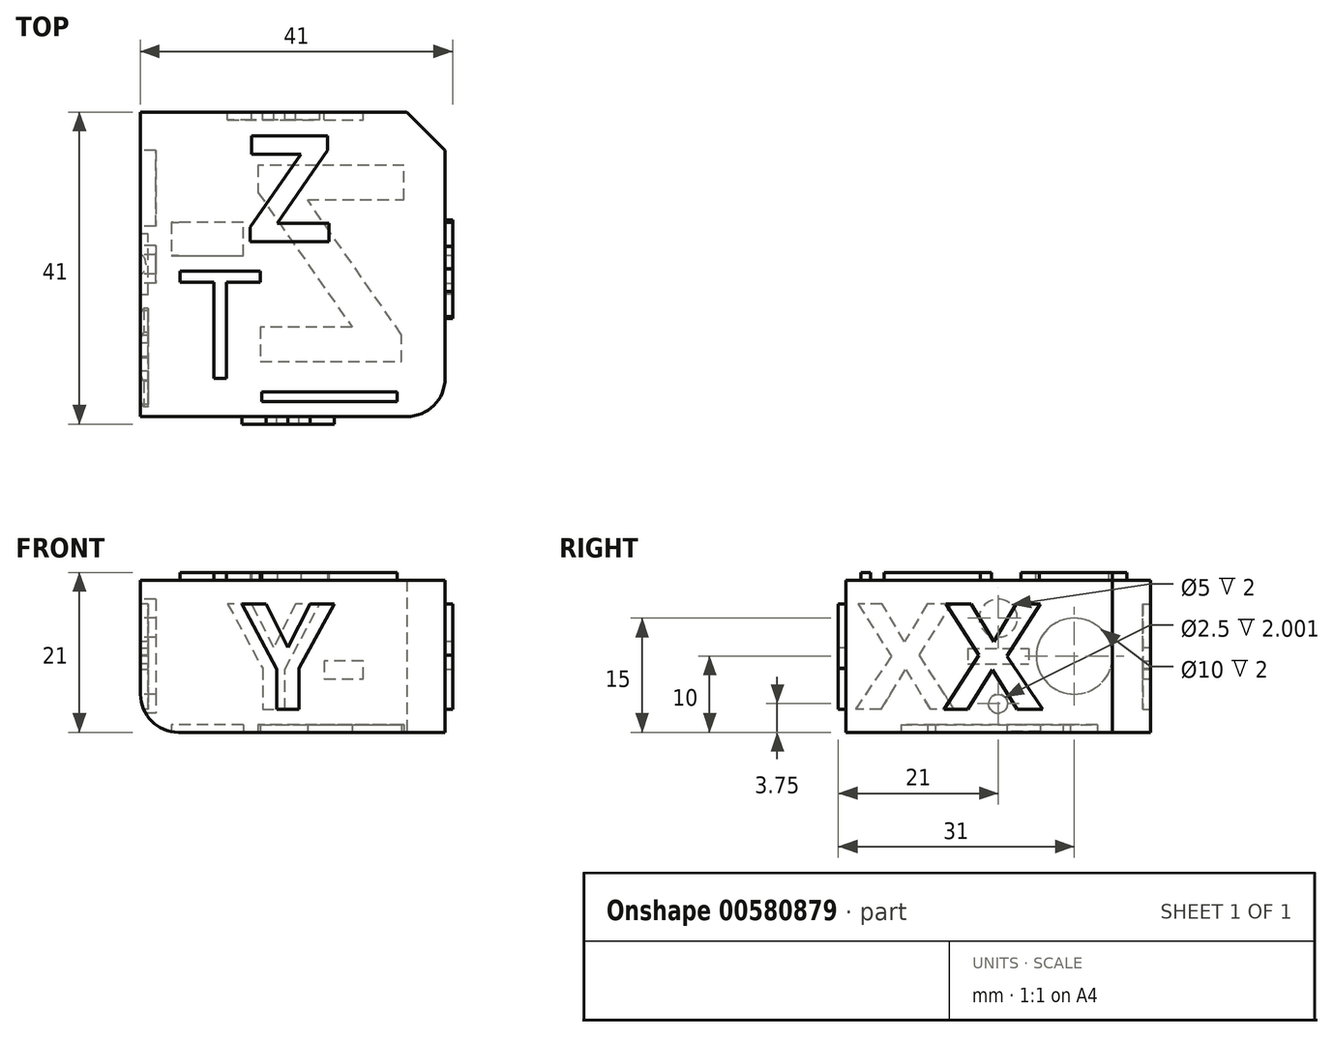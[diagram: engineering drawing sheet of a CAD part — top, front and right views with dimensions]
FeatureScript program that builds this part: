
annotation { "Feature Type Name" : "Feature", "Feature Type Description" : "" }
export const myFeature = defineFeature(function(context is Context, id is Id, definition is map)
    precondition{}
    {
        {
            var Q0;
            Q0=qCreatedBy(makeId("Top.planeOp"),FACE);
            var sketch = newSketch(context, id + "F0", { "sketchPlane" : qUnion([Q0])});
            skLineSegment(sketch, "E0.bottom", {"start": v(20, 20) * mm, "end": v(-20, 20) * mm});
            skLineSegment(sketch, "E0.top", {"start": v(20, -20) * mm, "end": v(-20, -20) * mm});
            skLineSegment(sketch, "E0.left", {"start": v(20, 20) * mm, "end": v(20, -20) * mm});
            skLineSegment(sketch, "E0.right", {"start": v(-20, 20) * mm, "end": v(-20, -20) * mm});
            skPoint(sketch, "E0.middle", {"position": v(0, 0) * mm});
            skSolve(sketch);
        }
        {
            var Q0;
            Q0=makeQuery(id+"F0.imprint","IMPRINT",FACE,{"disambiguationData":[TD([[makeQuery(id+"F0.imprint","IMPRINT",EDGE,{"derivedFrom":sQuery(id+"F0.wireOp",EDGE,"E0.bottom")}),1.0]])]});
            extrude(context, id + "F1", {"entities" : qUnion([Q0]), "depth" : 20 * mm, "offsetDistance" : 25 * mm});
        }
        {
            var Q0;
            Q0=makeQuery(id+"F1.opExtrude","SWEPT_EDGE",EDGE,{"disambiguationData":[OSD([sQuery(id+"F0.wireOp",EDGE,"E0.top"),sQuery(id+"F0.wireOp",EDGE,"E0.left")])]});
            fillet(context, id + "F2", {"entities" : qUnion([Q0]), "radius" : 5 * mm, "tangentPropagation" : true, "allowEdgeOverflow" : false});
        }
        {
            var Q0;
            Q0=makeQuery(id+"F1.opExtrude","SWEPT_EDGE",EDGE,{"disambiguationData":[OSD([sQuery(id+"F0.wireOp",EDGE,"E0.bottom"),sQuery(id+"F0.wireOp",EDGE,"E0.left")])]});
            chamfer(context, id + "F3", {"entities" : qUnion([Q0]), "width" : 5 * mm, "tangentPropagation" : true});
        }
        {
            var Q0;
            Q0=makeQuery(id+"F1.opExtrude","SWEPT_FACE",FACE,{"disambiguationData":[OSD([sQuery(id+"F0.wireOp",EDGE,"E0.top")])]});
            var sketch = newSketch(context, id + "F4", { "sketchPlane" : qUnion([Q0])});
            skText(sketch, "E1", { "text": "Y", "fontName": "OpenSans-Bold.ttf"});
            const initialGuessF4  = {"E1": [-0.0067, 0.003, 1, 0, 0.014]};
            skSetInitialGuess(sketch, initialGuessF4);
            skSolve(sketch);
        }
        {
            var Q0;
            Q0=makeQuery(id+"F4.imprint","IMPRINT",FACE,{"disambiguationData":[TD([[makeQuery(id+"F4.imprint","IMPRINT",EDGE,{"derivedFrom":sQuery(id+"F4.wireOp",EDGE,"E1.sketch_text.stroke-0")}),-1.0]])]});
            extrude(context, id + "F5", {"entities" : qUnion([Q0]), "operationType" : NewBodyOperationType.ADD, "depth" : 1 * mm, "offsetDistance" : 25 * mm});
        }
        {
            var Q0;
            Q0=makeQuery(id+"F1.opExtrude","SWEPT_FACE",FACE,{"disambiguationData":[OSD([sQuery(id+"F0.wireOp",EDGE,"E0.bottom")])]});
            var sketch = newSketch(context, id + "F6", { "sketchPlane" : qUnion([Q0])});
            skText(sketch, "E2", { "text": "-Y", "fontName": "OpenSans-Bold.ttf"});
            const initialGuessF6  = {"E2": [-0.00983, 0.003, 1, 0, 0.014]};
            skSetInitialGuess(sketch, initialGuessF6);
            skSolve(sketch);
        }
        {
            var Q0;
            Q0=makeQuery(id+"F6.imprint","IMPRINT",FACE,{"disambiguationData":[TD([[makeQuery(id+"F6.imprint","IMPRINT",EDGE,{"derivedFrom":sQuery(id+"F6.wireOp",EDGE,"E2.sketch_text.stroke-0")}),-1.0]])]});
            var Q1;
            Q1=makeQuery(id+"F6.imprint","IMPRINT",FACE,{"disambiguationData":[TD([[makeQuery(id+"F6.imprint","IMPRINT",EDGE,{"derivedFrom":sQuery(id+"F6.wireOp",EDGE,"E2.sketch_text.stroke-4")}),-1.0]])]});
            extrude(context, id + "F7", {"entities" : qUnion([Q0, Q1]), "operationType" : NewBodyOperationType.REMOVE, "oppositeDirection" : true, "depth" : 1 * mm, "offsetDistance" : 25 * mm});
        }
        {
            var Q0;
            Q0=makeQuery(id+"F1.opExtrude","SWEPT_FACE",FACE,{"disambiguationData":[OSD([sQuery(id+"F0.wireOp",EDGE,"E0.left")])]});
            var sketch = newSketch(context, id + "F8", { "sketchPlane" : qUnion([Q0])});
            skText(sketch, "E3", { "text": "X", "fontName": "OpenSans-Bold.ttf"});
            const initialGuessF8  = {"E3": [-0.00712, 0.003, 1, 0, 0.014]};
            skSetInitialGuess(sketch, initialGuessF8);
            skSolve(sketch);
        }
        {
            var Q0;
            Q0=makeQuery(id+"F8.imprint","IMPRINT",FACE,{"disambiguationData":[TD([[makeQuery(id+"F8.imprint","IMPRINT",EDGE,{"derivedFrom":sQuery(id+"F8.wireOp",EDGE,"E3.sketch_text.stroke-0")}),-1.0]])]});
            extrude(context, id + "F9", {"entities" : qUnion([Q0]), "operationType" : NewBodyOperationType.ADD, "depth" : 1 * mm, "offsetDistance" : 25 * mm});
        }
        {
            var Q0;
            Q0=makeQuery(id+"F1.opExtrude","SWEPT_FACE",FACE,{"disambiguationData":[OSD([sQuery(id+"F0.wireOp",EDGE,"E0.right")])]});
            var sketch = newSketch(context, id + "F10", { "sketchPlane" : qUnion([Q0])});
            skCircle(sketch, "E4", {"center": v(-10, 10) * mm, "radius": 5 * mm});
            skCircle(sketch, "E5", {"center": v(0, 15) * mm, "radius": 2.5 * mm});
            skCircle(sketch, "E6", {"center": v(0, 3.75) * mm, "radius": 1.25 * mm});
            skLineSegment(sketch, "E7.bottom", {"start": v(4, 11) * mm, "end": v(-4, 11) * mm});
            skLineSegment(sketch, "E7.top", {"start": v(4, 9) * mm, "end": v(-4, 9) * mm});
            skLineSegment(sketch, "E7.left", {"start": v(4, 11) * mm, "end": v(4, 9) * mm});
            skLineSegment(sketch, "E7.right", {"start": v(-4, 11) * mm, "end": v(-4, 9) * mm});
            skPoint(sketch, "E7.middle", {"position": v(0, 10) * mm});
            skText(sketch, "E8", { "text": "X", "fontName": "OpenSans-Bold.ttf"});
            const initialGuessF10  = {"E8": [0.00577, 0.003, 1, 0, 0.014]};
            skSetInitialGuess(sketch, initialGuessF10);
            skSolve(sketch);
        }
        {
            var Q0;
            Q0=makeQuery(id+"F10.imprint","IMPRINT",FACE,{"disambiguationData":[TD([[makeQuery(id+"F10.imprint","IMPRINT",EDGE,{"derivedFrom":sQuery(id+"F10.wireOp",EDGE,"E4")}),1.0]])]});
            var Q1;
            Q1=makeQuery(id+"F10.imprint","IMPRINT",FACE,{"disambiguationData":[TD([[makeQuery(id+"F10.imprint","IMPRINT",EDGE,{"derivedFrom":sQuery(id+"F10.wireOp",EDGE,"E6")}),1.0]])]});
            var Q2;
            Q2=makeQuery(id+"F10.imprint","IMPRINT",FACE,{"disambiguationData":[TD([[makeQuery(id+"F10.imprint","IMPRINT",EDGE,{"derivedFrom":sQuery(id+"F10.wireOp",EDGE,"E5")}),1.0]])]});
            extrude(context, id + "F11", {"entities" : qUnion([Q0, Q1, Q2]), "operationType" : NewBodyOperationType.REMOVE, "oppositeDirection" : true, "depth" : 2 * mm, "offsetDistance" : 25 * mm});
        }
        {
            var Q0;
            Q0=makeQuery(id+"F10.imprint","IMPRINT",FACE,{"disambiguationData":[TD([[makeQuery(id+"F10.imprint","IMPRINT",EDGE,{"derivedFrom":sQuery(id+"F10.wireOp",EDGE,"E7.bottom")}),1.0]])]});
            var Q1;
            Q1=makeQuery(id+"F10.imprint","IMPRINT",FACE,{"disambiguationData":[TD([[makeQuery(id+"F10.imprint","IMPRINT",EDGE,{"derivedFrom":sQuery(id+"F10.wireOp",EDGE,"E8.sketch_text.stroke-0")}),-1.0]])]});
            extrude(context, id + "F12", {"entities" : qUnion([Q0, Q1]), "operationType" : NewBodyOperationType.REMOVE, "oppositeDirection" : true, "depth" : 1 * mm, "offsetDistance" : 25 * mm});
        }
        {
            var Q0;
            Q0=makeQuery(id+"F1.opExtrude","CAP_FACE",FACE,{"disambiguationData":[OSD([sQuery(id+"F0.wireOp",EDGE,"E0.bottom"),sQuery(id+"F0.wireOp",EDGE,"E0.top"),sQuery(id+"F0.wireOp",EDGE,"E0.left"),sQuery(id+"F0.wireOp",EDGE,"E0.right")])],"isStart":false});
            var sketch = newSketch(context, id + "F13", { "sketchPlane" : qUnion([Q0])});
            skText(sketch, "E9", { "text": "T__", "fontName": "OpenSans-Regular.ttf"});
            skText(sketch, "E10", { "text": "Z", "fontName": "OpenSans-Bold.ttf"});
            const initialGuessF13  = {"E9": [-0.015, -0.015, 1, 0, 0.01424], "E10": [-0.00603, 0.003, 1, 0, 0.014]};
            skSetInitialGuess(sketch, initialGuessF13);
            skSolve(sketch);
        }
        {
            var Q0;
            Q0=makeQuery(id+"F13.imprint","IMPRINT",FACE,{"disambiguationData":[TD([[makeQuery(id+"F13.imprint","IMPRINT",EDGE,{"derivedFrom":sQuery(id+"F13.wireOp",EDGE,"E10.sketch_text.stroke-0")}),-1.0]])]});
            var Q1;
            Q1=makeQuery(id+"F13.imprint","IMPRINT",FACE,{"disambiguationData":[TD([[makeQuery(id+"F13.imprint","IMPRINT",EDGE,{"derivedFrom":sQuery(id+"F13.wireOp",EDGE,"E9.sketch_text.stroke-0")}),-1.0]])]});
            var Q2;
            {var subQ0=sQuery(id+"F13.wireOp",EDGE,"E9.sketch_text.stroke-11");Q2=makeQuery(id+"F13.imprint","IMPRINT",FACE,{"disambiguationData":[TD([[makeQuery(id+"F13.imprint","IMPRINT",EDGE,{"derivedFrom":subQ0}),1.0]])]});}
            var Q3;
            Q3=makeQuery(id+"F13.imprint","IMPRINT",FACE,{"disambiguationData":[TD([[makeQuery(id+"F13.imprint","IMPRINT",EDGE,{"derivedFrom":sQuery(id+"F13.wireOp",EDGE,"E9.sketch_text.stroke-8")}),-1.0]])]});
            var Q4;
            {var subQ0=sQuery(id+"F13.wireOp",EDGE,"E9.sketch_text.stroke-11");Q4=makeQuery(id+"F13.imprint","IMPRINT",FACE,{"disambiguationData":[TD([[makeQuery(id+"F13.imprint","IMPRINT",EDGE,{"derivedFrom":subQ0}),-1.0]])]});}
            extrude(context, id + "F14", {"entities" : qUnion([Q0, Q1, Q2, Q3, Q4]), "operationType" : NewBodyOperationType.ADD, "depth" : 1 * mm, "offsetDistance" : 25 * mm});
        }
        {
            var Q0;
            Q0=makeQuery(id+"F1.opExtrude","CAP_FACE",FACE,{"disambiguationData":[OSD([sQuery(id+"F0.wireOp",EDGE,"E0.bottom"),sQuery(id+"F0.wireOp",EDGE,"E0.top"),sQuery(id+"F0.wireOp",EDGE,"E0.left"),sQuery(id+"F0.wireOp",EDGE,"E0.right")])],"isStart":true});
            var sketch = newSketch(context, id + "F15", { "sketchPlane" : qUnion([Q0])});
            skText(sketch, "E11", { "text": "-Z", "fontName": "OpenSans-Bold.ttf"});
            const initialGuessF15  = {"E11": [-0.01705, -0.013, 1, 0, 0.026]};
            skSetInitialGuess(sketch, initialGuessF15);
            skSolve(sketch);
        }
        {
            var Q0;
            Q0=makeQuery(id+"F15.imprint","IMPRINT",FACE,{"disambiguationData":[TD([[makeQuery(id+"F15.imprint","IMPRINT",EDGE,{"derivedFrom":sQuery(id+"F15.wireOp",EDGE,"E11.sketch_text.stroke-4")}),-1.0]])]});
            var Q1;
            Q1=makeQuery(id+"F15.imprint","IMPRINT",FACE,{"disambiguationData":[TD([[makeQuery(id+"F15.imprint","IMPRINT",EDGE,{"derivedFrom":sQuery(id+"F15.wireOp",EDGE,"E11.sketch_text.stroke-0")}),-1.0]])]});
            extrude(context, id + "F16", {"entities" : qUnion([Q0, Q1]), "operationType" : NewBodyOperationType.REMOVE, "oppositeDirection" : true, "depth" : 1 * mm, "offsetDistance" : 25 * mm});
        }
        {
            var Q0;
            Q0=makeQuery(id+"F1.opExtrude","CAP_EDGE",EDGE,{"disambiguationData":[OSD([sQuery(id+"F0.wireOp",EDGE,"E0.right")])],"isStart":true});
            fillet(context, id + "F17", {"entities" : qUnion([Q0]), "radius" : 5 * mm, "tangentPropagation" : true, "allowEdgeOverflow" : false});
        }
    });
